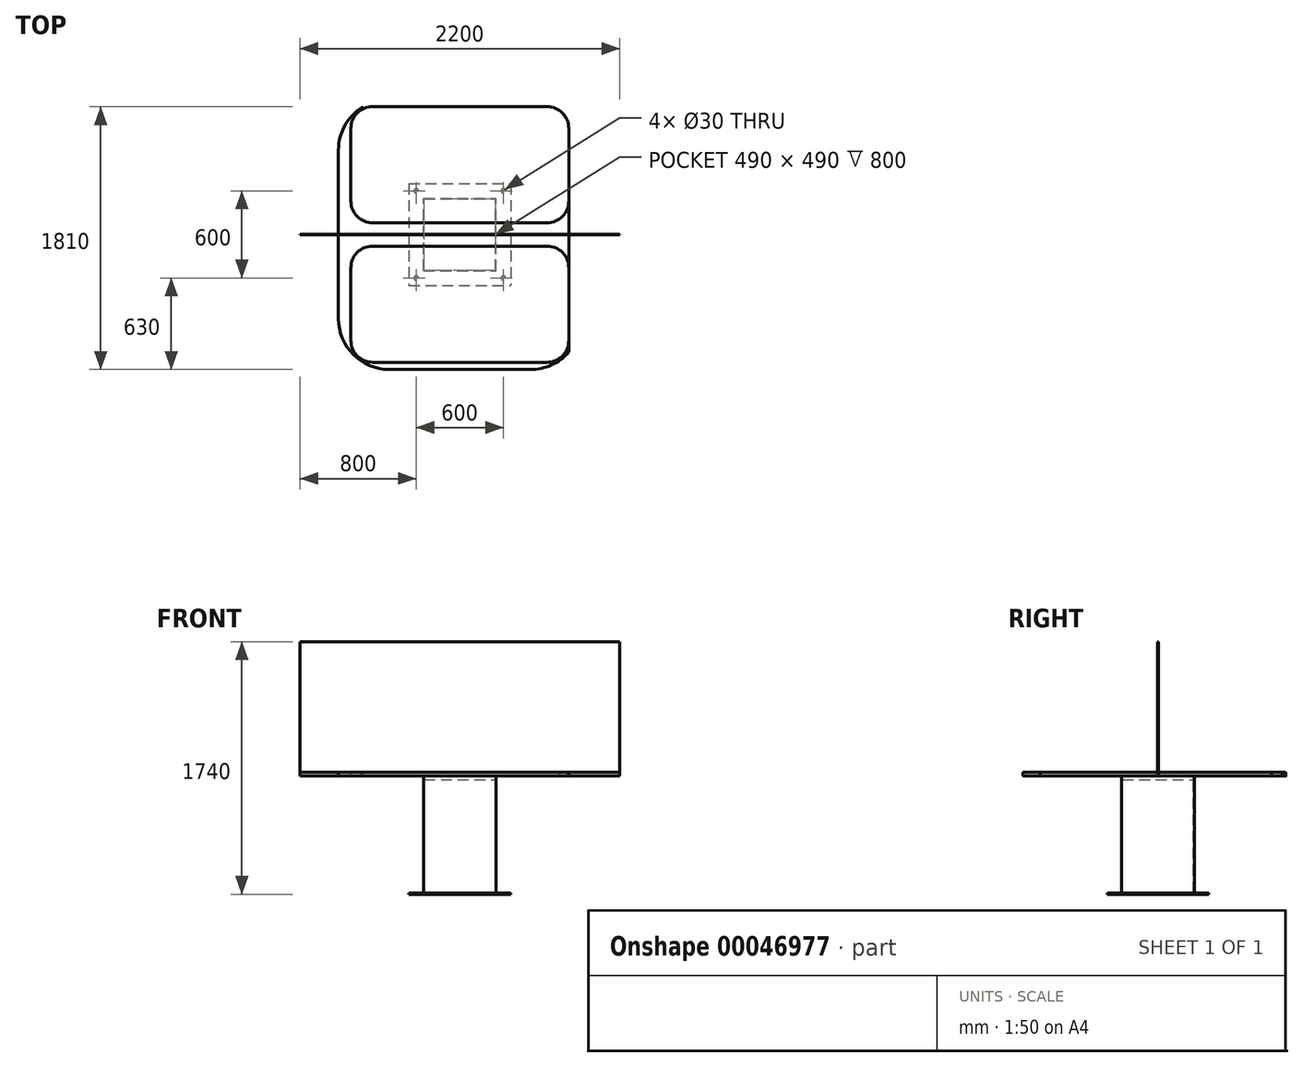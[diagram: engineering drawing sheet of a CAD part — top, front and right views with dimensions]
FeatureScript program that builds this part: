
annotation { "Feature Type Name" : "Feature", "Feature Type Description" : "" }
export const myFeature = defineFeature(function(context is Context, id is Id, definition is map)
    precondition{}
    {
        {
            var Q0;
            Q0=qCreatedBy(makeId("Top.planeOp"),FACE);
            var sketch = newSketch(context, id + "F0", { "sketchPlane" : qUnion([Q0])});
            skCircle(sketch, "E0", {"center": v(0, 0) * mm, "radius": 1250 * mm});
            skSolve(sketch);
        }
        {
            var Q0;
            Q0=qSketchRegion(id+"F0",true);
            extrude(context, id + "F1", {"entities" : qUnion([Q0]), "depth" : 25 * mm});
        }
        {
            var Q0;
            Q0=makeQuery(id+"F1.opExtrude","CAP_FACE",FACE,{"disambiguationData":[OSD([sQuery(id+"F0.wireOp",EDGE,"E0")])],"isStart":false});
            var sketch = newSketch(context, id + "F2", { "sketchPlane" : qUnion([Q0])});
            skLineSegment(sketch, "E1", {"start": v(0, 1250) * mm, "end": v(0, -1250) * mm, "construction": true});
            skLineSegment(sketch, "E2", {"start": v(149.27, 480) * mm, "end": v(0, 480) * mm, "construction": true});
            skLineSegment(sketch, "E3.MirrorCS", {"start": v(149.27, -480) * mm, "end": v(0, -480) * mm, "construction": true});
            skLineSegment(sketch, "E4.rect.bottom", {"start": v(600, 80) * mm, "end": v(-600, 80) * mm});
            skLineSegment(sketch, "E4.rect.top", {"start": v(600, 880) * mm, "end": v(-600, 880) * mm});
            skLineSegment(sketch, "E4.rect.left", {"start": v(750, 230) * mm, "end": v(750, 730) * mm});
            skLineSegment(sketch, "E4.rect.right", {"start": v(-750, 230) * mm, "end": v(-750, 730) * mm});
            skPoint(sketch, "E4.rect.middle", {"position": v(0, 480) * mm});
            skLineSegment(sketch, "E5.MirrorCS", {"start": v(-750, -230) * mm, "end": v(-750, -730) * mm});
            skLineSegment(sketch, "E6.MirrorCS", {"start": v(750, -230) * mm, "end": v(750, -730) * mm});
            skLineSegment(sketch, "E7.MirrorCS", {"start": v(600, -880) * mm, "end": v(-600, -880) * mm});
            skLineSegment(sketch, "E8.MirrorCS", {"start": v(600, -80) * mm, "end": v(-600, -80) * mm});
            skLineSegment(sketch, "E9.MirrorCS", {"start": v(149.27, -480) * mm, "end": v(0, -480) * mm});
            skPoint(sketch, "E10.MirrorP", {"position": v(0, -480) * mm});
            skPoint(sketch, "E11.visualSharp", {"position": v(-750, -880) * mm});
            skArc(sketch, "E11.filletArc", {"start": v(-750, -730) * mm, "mid": v(-706.07, -836.07) * mm, "end": v(-600, -880) * mm});
            skPoint(sketch, "E12.visualSharp", {"position": v(-750, -80) * mm});
            skArc(sketch, "E12.filletArc", {"start": v(-600, -80) * mm, "mid": v(-706.07, -123.93) * mm, "end": v(-750, -230) * mm});
            skPoint(sketch, "E13.visualSharp", {"position": v(750, -80) * mm});
            skArc(sketch, "E13.filletArc", {"start": v(750, -230) * mm, "mid": v(706.07, -123.93) * mm, "end": v(600, -80) * mm});
            skPoint(sketch, "E14.visualSharp", {"position": v(750, -880) * mm});
            skArc(sketch, "E14.filletArc", {"start": v(600, -880) * mm, "mid": v(706.07, -836.07) * mm, "end": v(750, -730) * mm});
            skPoint(sketch, "E15.visualSharp", {"position": v(-750, 80) * mm});
            skArc(sketch, "E15.filletArc", {"start": v(-750, 230) * mm, "mid": v(-706.07, 123.93) * mm, "end": v(-600, 80) * mm});
            skPoint(sketch, "E16.visualSharp", {"position": v(-750, 880) * mm});
            skArc(sketch, "E16.filletArc", {"start": v(-600, 880) * mm, "mid": v(-706.07, 836.07) * mm, "end": v(-750, 730) * mm});
            skPoint(sketch, "E17.visualSharp", {"position": v(750, 880) * mm});
            skArc(sketch, "E17.filletArc", {"start": v(750, 730) * mm, "mid": v(706.07, 836.07) * mm, "end": v(600, 880) * mm});
            skPoint(sketch, "E18.visualSharp", {"position": v(750, 80) * mm});
            skArc(sketch, "E18.filletArc", {"start": v(600, 80) * mm, "mid": v(706.07, 123.93) * mm, "end": v(750, 230) * mm});
            skSolve(sketch);
        }
        {
            var Q0;
            Q0=makeQuery(id+"F2.imprint","IMPRINT",FACE,{"disambiguationData":[TD([[makeQuery(id+"F2.imprint","IMPRINT",EDGE,{"derivedFrom":sQuery(id+"F2.wireOp",EDGE,"E4.rect.bottom")}),-1.0]])]});
            var Q1;
            Q1=makeQuery(id+"F2.imprint","IMPRINT",FACE,{"disambiguationData":[TD([[makeQuery(id+"F2.imprint","IMPRINT",EDGE,{"derivedFrom":sQuery(id+"F2.wireOp",EDGE,"E5.MirrorCS")}),1.0]])]});
            extrude(context, id + "F3", {"entities" : qUnion([Q0, Q1]), "operationType" : NewBodyOperationType.ADD, "depth" : 0.1 * mm});
        }
        {
            var Q0;
            Q0=makeQuery(id+"F1.opExtrude","CAP_FACE",FACE,{"disambiguationData":[OSD([sQuery(id+"F0.wireOp",EDGE,"E0")])],"isStart":true});
            var sketch = newSketch(context, id + "F4", { "sketchPlane" : qUnion([Q0])});
            skLineSegment(sketch, "E19.rect.bottom", {"start": v(-250, 250) * mm, "end": v(250, 250) * mm});
            skLineSegment(sketch, "E19.rect.top", {"start": v(-250, -250) * mm, "end": v(250, -250) * mm});
            skLineSegment(sketch, "E19.rect.left", {"start": v(-250, 250) * mm, "end": v(-250, -250) * mm});
            skLineSegment(sketch, "E19.rect.right", {"start": v(250, 250) * mm, "end": v(250, -250) * mm});
            skPoint(sketch, "E19.rect.middle", {"position": v(0, 0) * mm});
            skLineSegment(sketch, "E20.rect.bottom", {"start": v(-245, 245) * mm, "end": v(245, 245) * mm});
            skLineSegment(sketch, "E20.rect.top", {"start": v(-245, -245) * mm, "end": v(245, -245) * mm});
            skLineSegment(sketch, "E20.rect.left", {"start": v(-245, 245) * mm, "end": v(-245, -245) * mm});
            skLineSegment(sketch, "E20.rect.right", {"start": v(245, 245) * mm, "end": v(245, -245) * mm});
            skSolve(sketch);
        }
        {
            var Q0;
            Q0=makeQuery(id+"F4.imprint","IMPRINT",FACE,{"disambiguationData":[TD([[makeQuery(id+"F4.imprint","IMPRINT",EDGE,{"derivedFrom":sQuery(id+"F4.wireOp",EDGE,"E19.rect.bottom")}),-1.0]])]});
            extrude(context, id + "F5", {"entities" : qUnion([Q0]), "depth" : 800 * mm});
        }
        {
            var Q0;
            Q0=makeQuery(id+"F1.opExtrude","CAP_FACE",FACE,{"disambiguationData":[OSD([sQuery(id+"F0.wireOp",EDGE,"E0")])],"isStart":false});
            var sketch = newSketch(context, id + "F6", { "sketchPlane" : qUnion([Q0])});
            skLineSegment(sketch, "E21.rect.left", {"start": v(-1250, 2.5) * mm, "end": v(-1250, -2.5) * mm});
            skLineSegment(sketch, "E21.rect.right", {"start": v(1250, 2.5) * mm, "end": v(1250, -2.5) * mm});
            skPoint(sketch, "E21.rect.middle", {"position": v(0, 0) * mm});
            skLineSegment(sketch, "E22.rect.bottom", {"start": v(1100, -2.5) * mm, "end": v(-1100, -2.5) * mm});
            skLineSegment(sketch, "E22.rect.top", {"start": v(1100, 2.5) * mm, "end": v(-1100, 2.5) * mm});
            skLineSegment(sketch, "E22.rect.left", {"start": v(1100, -2.5) * mm, "end": v(1100, 2.5) * mm});
            skLineSegment(sketch, "E22.rect.right", {"start": v(-1100, -2.5) * mm, "end": v(-1100, 2.5) * mm});
            skSolve(sketch);
        }
        {
            var Q0;
            Q0=makeQuery(id+"F6.imprint","IMPRINT",FACE,{"disambiguationData":[TD([[makeQuery(id+"F6.imprint","IMPRINT",EDGE,{"derivedFrom":sQuery(id+"F6.wireOp",EDGE,"E21.rect.bottom")}),-1.0]])]});
            var Q1;
            Q1=makeQuery(id+"F6.imprint","IMPRINT",FACE,{"disambiguationData":[TD([[makeQuery(id+"F6.imprint","IMPRINT",EDGE,{"derivedFrom":sQuery(id+"F6.wireOp",EDGE,"E22.rect.bottom")}),-1.0]])]});
            extrude(context, id + "F7", {"entities" : qUnion([Q0, Q1]), "depth" : 900 * mm});
        }
        {
            var Q0;
            Q0=makeQuery(id+"F5.opExtrude","CAP_FACE",FACE,{"disambiguationData":[OSD([sQuery(id+"F4.wireOp",EDGE,"E19.rect.bottom"),sQuery(id+"F4.wireOp",EDGE,"E19.rect.top"),sQuery(id+"F4.wireOp",EDGE,"E19.rect.left"),sQuery(id+"F4.wireOp",EDGE,"E19.rect.right"),sQuery(id+"F4.wireOp",EDGE,"E20.rect.bottom"),sQuery(id+"F4.wireOp",EDGE,"E20.rect.top"),sQuery(id+"F4.wireOp",EDGE,"E20.rect.left"),sQuery(id+"F4.wireOp",EDGE,"E20.rect.right")])],"isStart":false});
            var sketch = newSketch(context, id + "F8", { "sketchPlane" : qUnion([Q0])});
            skLineSegment(sketch, "E23.bottom", {"start": v(-250, 250) * mm, "end": v(250, 250) * mm});
            skLineSegment(sketch, "E23.top", {"start": v(-250, -250) * mm, "end": v(250, -250) * mm});
            skLineSegment(sketch, "E23.left", {"start": v(-250, 250) * mm, "end": v(-250, -250) * mm});
            skLineSegment(sketch, "E23.right", {"start": v(250, 250) * mm, "end": v(250, -250) * mm});
            skSolve(sketch);
        }
        {
            var Q0;
            Q0=qSketchRegion(id+"F8",true);
            extrude(context, id + "F9", {"entities" : qUnion([Q0]), "operationType" : NewBodyOperationType.ADD, "depth" : 5 * mm});
        }
        {
            var Q0;
            Q0=makeQuery(id+"F9.opExtrude","CAP_FACE",FACE,{"disambiguationData":[OSD([sQuery(id+"F8.wireOp",EDGE,"E23.bottom"),sQuery(id+"F8.wireOp",EDGE,"E23.top"),sQuery(id+"F8.wireOp",EDGE,"E23.left"),sQuery(id+"F8.wireOp",EDGE,"E23.right")])],"isStart":false});
            var sketch = newSketch(context, id + "F10", { "sketchPlane" : qUnion([Q0])});
            skLineSegment(sketch, "E24.rect.bottom", {"start": v(-350, -350) * mm, "end": v(350, -350) * mm});
            skLineSegment(sketch, "E24.rect.top", {"start": v(-350, 350) * mm, "end": v(350, 350) * mm});
            skLineSegment(sketch, "E24.rect.left", {"start": v(-350, -350) * mm, "end": v(-350, 350) * mm});
            skLineSegment(sketch, "E24.rect.right", {"start": v(350, -350) * mm, "end": v(350, 350) * mm});
            skPoint(sketch, "E24.rect.middle", {"position": v(0, 0) * mm});
            skLineSegment(sketch, "E25.rect.bottom", {"start": v(-300, 300) * mm, "end": v(300, 300) * mm, "construction": true});
            skLineSegment(sketch, "E25.rect.top", {"start": v(-300, -300) * mm, "end": v(300, -300) * mm, "construction": true});
            skLineSegment(sketch, "E25.rect.left", {"start": v(-300, 300) * mm, "end": v(-300, -300) * mm, "construction": true});
            skLineSegment(sketch, "E25.rect.right", {"start": v(300, 300) * mm, "end": v(300, -300) * mm, "construction": true});
            skCircle(sketch, "E26", {"center": v(-300, 300) * mm, "radius": 15 * mm});
            skCircle(sketch, "E27", {"center": v(300, 300) * mm, "radius": 15 * mm});
            skCircle(sketch, "E28", {"center": v(300, -300) * mm, "radius": 15 * mm});
            skCircle(sketch, "E29", {"center": v(-300, -300) * mm, "radius": 15 * mm});
            skSolve(sketch);
        }
        {
            var Q0;
            Q0=qSketchRegion(id+"F10",true);
            extrude(context, id + "F11", {"entities" : qUnion([Q0]), "operationType" : NewBodyOperationType.ADD, "depth" : 10 * mm});
        }
        {
            var Q0;
            Q0=makeQuery(id+"F1.opExtrude","CAP_FACE",FACE,{"disambiguationData":[OSD([sQuery(id+"F0.wireOp",EDGE,"E0")])],"isStart":false});
            var sketch = newSketch(context, id + "F12", { "sketchPlane" : qUnion([Q0])});
            skLineSegment(sketch, "E30", {"start": v(1245, 930) * mm, "end": v(-1255, 930) * mm});
            skLineSegment(sketch, "E31", {"start": v(-1255, 930) * mm, "end": v(-1255, 1430) * mm});
            skLineSegment(sketch, "E32", {"start": v(-1255, 1430) * mm, "end": v(1245, 1430) * mm});
            skLineSegment(sketch, "E33", {"start": v(1245, 1430) * mm, "end": v(1245, 930) * mm});
            skLineSegment(sketch, "E34", {"start": v(0, 0) * mm, "end": v(209.4, 0) * mm});
            skLineSegment(sketch, "E35.MirrorCS", {"start": v(1245, -930) * mm, "end": v(-1255, -930) * mm});
            skLineSegment(sketch, "E36.MirrorCS", {"start": v(-1255, -930) * mm, "end": v(-1255, -1430) * mm});
            skLineSegment(sketch, "E37.MirrorCS", {"start": v(-1255, -1430) * mm, "end": v(1245, -1430) * mm});
            skLineSegment(sketch, "E38.MirrorCS", {"start": v(1245, -1430) * mm, "end": v(1245, -930) * mm});
            skSolve(sketch);
        }
        {
            var Q0;
            {var subQ5=sQuery(id+"F12.wireOp",EDGE,"E36.MirrorCS");Q0=makeQuery(id+"F12.imprint","IMPRINT",FACE,{"disambiguationData":[TD([[makeQuery(id+"F12.imprint","IMPRINT",EDGE,{"derivedFrom":subQ5}),1.0]])]});}
            var Q1;
            {var subQ0=makeQuery(id+"F1.opExtrude","CAP_EDGE",EDGE,{"disambiguationData":[OSD([sQuery(id+"F0.wireOp",EDGE,"E0")])],"isStart":false});var subQ1=sQuery(id+"F12.wireOp",EDGE,"E30");var subQ3=makeQuery(id+"F12.imprint","INTERSECT",VERTEX,{"disambiguationData":[OD(0.0)],"derivedFrom":[subQ0,subQ1]});Q1=makeQuery(id+"F12.imprint","IMPRINT",FACE,{"disambiguationData":[TD([[makeQuery(id+"F12.imprint","IMPRINT",EDGE,{"disambiguationData":[TD([[subQ3,-1.0]])],"derivedFrom":subQ1}),-1.0]])]});}
            var Q2;
            {var subQ0=makeQuery(id+"F1.opExtrude","CAP_EDGE",EDGE,{"disambiguationData":[OSD([sQuery(id+"F0.wireOp",EDGE,"E0")])],"isStart":false});var subQ1=sQuery(id+"F12.wireOp",EDGE,"E35.MirrorCS");var subQ3=makeQuery(id+"F12.imprint","INTERSECT",VERTEX,{"disambiguationData":[OD(0.0)],"derivedFrom":[subQ0,subQ1]});Q2=makeQuery(id+"F12.imprint","IMPRINT",FACE,{"disambiguationData":[TD([[makeQuery(id+"F12.imprint","IMPRINT",EDGE,{"disambiguationData":[TD([[subQ3,-1.0]])],"derivedFrom":subQ1}),1.0]])]});}
            extrude(context, id + "F13", {"entities" : qUnion([Q0, Q1, Q2]), "operationType" : NewBodyOperationType.REMOVE, "oppositeDirection" : true, "depth" : 30 * mm});
        }
        {
            var Q0;
            Q0=makeQuery(id+"F1.opExtrude","CAP_FACE",FACE,{"disambiguationData":[OSD([sQuery(id+"F0.wireOp",EDGE,"E0")])],"isStart":false});
            var sketch = newSketch(context, id + "F14", { "sketchPlane" : qUnion([Q0])});
            skLineSegment(sketch, "E39", {"start": v(835.22, -930) * mm, "end": v(835.22, 930) * mm});
            skLineSegment(sketch, "E40", {"start": v(835.22, 930) * mm, "end": v(1324.29, 930) * mm});
            skLineSegment(sketch, "E41", {"start": v(1324.29, 930) * mm, "end": v(1324.29, -826) * mm});
            skLineSegment(sketch, "E42", {"start": v(1324.29, -826) * mm, "end": v(835.22, -930) * mm});
            skLineSegment(sketch, "E43.MirrorCS", {"start": v(-835.22, -930) * mm, "end": v(-835.22, 930) * mm});
            skLineSegment(sketch, "E44.MirrorCS", {"start": v(-835.22, 930) * mm, "end": v(-1324.29, 930) * mm});
            skLineSegment(sketch, "E45.MirrorCS", {"start": v(-1324.29, 930) * mm, "end": v(-1324.29, -826) * mm});
            skLineSegment(sketch, "E46.MirrorCS", {"start": v(-1324.29, -826) * mm, "end": v(-835.22, -930) * mm});
            skSolve(sketch);
        }
        {
            var Q0;
            Q0=qSketchRegion(id+"F14",true);
            extrude(context, id + "F15", {"entities" : qUnion([Q0]), "operationType" : NewBodyOperationType.REMOVE, "oppositeDirection" : true, "depth" : 30 * mm});
        }
        {
            var Q0;
            Q0=makeQuery(id+"F5.opExtrude","CAP_FACE",FACE,{"disambiguationData":[OSD([sQuery(id+"F4.wireOp",EDGE,"E19.rect.bottom"),sQuery(id+"F4.wireOp",EDGE,"E19.rect.top"),sQuery(id+"F4.wireOp",EDGE,"E19.rect.left"),sQuery(id+"F4.wireOp",EDGE,"E19.rect.right"),sQuery(id+"F4.wireOp",EDGE,"E20.rect.bottom"),sQuery(id+"F4.wireOp",EDGE,"E20.rect.top"),sQuery(id+"F4.wireOp",EDGE,"E20.rect.left"),sQuery(id+"F4.wireOp",EDGE,"E20.rect.right")])],"isStart":true});
            var sketch = newSketch(context, id + "F16", { "sketchPlane" : qUnion([Q0])});
            skLineSegment(sketch, "E47.bottom", {"start": v(-245, 245) * mm, "end": v(245, 245) * mm});
            skLineSegment(sketch, "E47.top", {"start": v(-245, -245) * mm, "end": v(245, -245) * mm});
            skLineSegment(sketch, "E47.left", {"start": v(-245, 245) * mm, "end": v(-245, -245) * mm});
            skLineSegment(sketch, "E47.right", {"start": v(245, 245) * mm, "end": v(245, -245) * mm});
            skSolve(sketch);
        }
        {
            var Q0;
            Q0=qSketchRegion(id+"F16",true);
            extrude(context, id + "F17", {"entities" : qUnion([Q0]), "oppositeDirection" : true, "depth" : 25 * mm});
        }
        {
            var Q0;
            {var subQ0=sQuery(id+"F0.wireOp",EDGE,"E0");var subQ1=sQuery(id+"F12.wireOp",EDGE,"E30");Q0=makeQuery(id+"F15.boolean.opBoolean","MERGE",EDGE,{"derivedFrom":[makeQuery(id+"F13.boolean.opBoolean","COPY",EDGE,{"derivedFrom":makeQuery(id+"F13.opExtrude","SWEPT_EDGE",EDGE,{"disambiguationData":[OSD([subQ0,subQ1]),TDD([makeQuery(id+"F12.imprint","INTERSECT",VERTEX,{"disambiguationData":[OD(1.0)],"derivedFrom":[makeQuery(id+"F1.opExtrude","CAP_EDGE",EDGE,{"disambiguationData":[OSD([subQ0])],"isStart":false}),subQ1]})])]})}),makeQuery(id+"F15.opExtrude","SWEPT_EDGE",EDGE,{"disambiguationData":[OSD([subQ0,subQ1,sQuery(id+"F14.wireOp",EDGE,"E43.MirrorCS"),sQuery(id+"F14.wireOp",EDGE,"E44.MirrorCS")])]})]});}
            var Q1;
            {var subQ0=sQuery(id+"F0.wireOp",EDGE,"E0");var subQ1=sQuery(id+"F12.wireOp",EDGE,"E35.MirrorCS");Q1=makeQuery(id+"F15.boolean.opBoolean","MERGE",EDGE,{"derivedFrom":[makeQuery(id+"F13.boolean.opBoolean","INTERSECT",EDGE,{"disambiguationData":[OD(1.0)],"derivedFrom":[makeQuery(id+"F1.opExtrude","SWEPT_FACE",FACE,{"disambiguationData":[OSD([subQ0])]}),makeQuery(id+"F13.opExtrude","SWEPT_FACE",FACE,{"disambiguationData":[OSD([subQ1])]})]}),makeQuery(id+"F15.opExtrude","SWEPT_EDGE",EDGE,{"disambiguationData":[OSD([subQ0,subQ1,sQuery(id+"F14.wireOp",EDGE,"E43.MirrorCS"),sQuery(id+"F14.wireOp",EDGE,"E46.MirrorCS")])]})]});}
            var Q2;
            {var subQ0=sQuery(id+"F0.wireOp",EDGE,"E0");var subQ1=sQuery(id+"F12.wireOp",EDGE,"E35.MirrorCS");Q2=makeQuery(id+"F15.boolean.opBoolean","MERGE",EDGE,{"derivedFrom":[makeQuery(id+"F13.boolean.opBoolean","INTERSECT",EDGE,{"disambiguationData":[OD(0.0)],"derivedFrom":[makeQuery(id+"F1.opExtrude","SWEPT_FACE",FACE,{"disambiguationData":[OSD([subQ0])]}),makeQuery(id+"F13.opExtrude","SWEPT_FACE",FACE,{"disambiguationData":[OSD([subQ1])]})]}),makeQuery(id+"F15.opExtrude","SWEPT_EDGE",EDGE,{"disambiguationData":[OSD([subQ0,subQ1,sQuery(id+"F14.wireOp",EDGE,"E39"),sQuery(id+"F14.wireOp",EDGE,"E42")])]})]});}
            var Q3;
            {var subQ0=sQuery(id+"F0.wireOp",EDGE,"E0");var subQ1=sQuery(id+"F12.wireOp",EDGE,"E30");Q3=makeQuery(id+"F15.boolean.opBoolean","MERGE",EDGE,{"derivedFrom":[makeQuery(id+"F13.boolean.opBoolean","COPY",EDGE,{"derivedFrom":makeQuery(id+"F13.opExtrude","SWEPT_EDGE",EDGE,{"disambiguationData":[OSD([subQ0,subQ1]),TDD([makeQuery(id+"F12.imprint","INTERSECT",VERTEX,{"disambiguationData":[OD(0.0)],"derivedFrom":[makeQuery(id+"F1.opExtrude","CAP_EDGE",EDGE,{"disambiguationData":[OSD([subQ0])],"isStart":false}),subQ1]})])]})}),makeQuery(id+"F15.opExtrude","SWEPT_EDGE",EDGE,{"disambiguationData":[OSD([subQ0,subQ1,sQuery(id+"F14.wireOp",EDGE,"E39"),sQuery(id+"F14.wireOp",EDGE,"E40")])]})]});}
            fillet(context, id + "F18", {"entities" : qUnion([Q0, Q1, Q2, Q3]), "radius" : 350 * mm, "tangentPropagation" : true, "allowEdgeOverflow" : false});
        }
        {
            var Q0;
            Q0=makeQuery(id+"F1.opExtrude","CAP_FACE",FACE,{"disambiguationData":[OSD([sQuery(id+"F0.wireOp",EDGE,"E0")])],"isStart":false});
            var sketch = newSketch(context, id + "F19", { "sketchPlane" : qUnion([Q0])});
            skLineSegment(sketch, "E48", {"start": v(-750, 730) * mm, "end": v(-750, -730) * mm});
            skLineSegment(sketch, "E49", {"start": v(-750, -730) * mm, "end": v(-750, -880) * mm});
            skLineSegment(sketch, "E50", {"start": v(-750, -880) * mm, "end": v(750, -880) * mm});
            skLineSegment(sketch, "E51", {"start": v(750, -880) * mm, "end": v(750, 769.39) * mm});
            skLineSegment(sketch, "E52", {"start": v(-600, 880) * mm, "end": v(665.5, 880) * mm});
            skLineSegment(sketch, "E53", {"start": v(665.5, 880) * mm, "end": v(750, 769.39) * mm});
            skLineSegment(sketch, "E54", {"start": v(-600, 880) * mm, "end": v(-665.5, 880) * mm});
            skLineSegment(sketch, "E55", {"start": v(-665.5, 880) * mm, "end": v(-750, 730) * mm});
            skSolve(sketch);
        }
        {
            var Q0;
            {var subQ2=sQuery(id+"F14.wireOp",EDGE,"E43.MirrorCS");var subQ7=makeQuery(id+"F15.boolean.opBoolean","COPY",EDGE,{"derivedFrom":makeQuery(id+"F15.opExtrude","CAP_EDGE",EDGE,{"disambiguationData":[OSD([subQ2])],"isStart":true})});Q0=makeQuery(id+"F19.imprint","IMPRINT",FACE,{"disambiguationData":[TD([[makeQuery(id+"F19.imprint","IMPRINT",EDGE,{"derivedFrom":subQ7}),-1.0]])]});}
            var Q1;
            {var subQ5=sQuery(id+"F19.wireOp",EDGE,"E54");Q1=makeQuery(id+"F19.imprint","IMPRINT",FACE,{"disambiguationData":[TD([[makeQuery(id+"F19.imprint","IMPRINT",EDGE,{"derivedFrom":subQ5}),-1.0]])]});}
            var Q2;
            {var subQ8=sQuery(id+"F19.wireOp",EDGE,"E53");Q2=makeQuery(id+"F19.imprint","IMPRINT",FACE,{"disambiguationData":[TD([[makeQuery(id+"F19.imprint","IMPRINT",EDGE,{"derivedFrom":subQ8}),1.0]])]});}
            var Q3;
            {var subQ2=sQuery(id+"F12.wireOp",EDGE,"E35.MirrorCS");var subQ8=makeQuery(id+"F13.boolean.opBoolean","COPY",EDGE,{"derivedFrom":makeQuery(id+"F13.opExtrude","CAP_EDGE",EDGE,{"disambiguationData":[OSD([subQ2])],"isStart":true})});Q3=makeQuery(id+"F19.imprint","IMPRINT",FACE,{"disambiguationData":[TD([[makeQuery(id+"F19.imprint","IMPRINT",EDGE,{"derivedFrom":subQ8}),-1.0]])]});}
            var Q4;
            {var subQ7=makeQuery(id+"F3.opExtrude","CAP_EDGE",EDGE,{"disambiguationData":[OSD([sQuery(id+"F2.wireOp",EDGE,"E14.filletArc")])],"isStart":true});Q4=makeQuery(id+"F19.imprint","IMPRINT",FACE,{"disambiguationData":[TD([[makeQuery(id+"F19.imprint","IMPRINT",EDGE,{"derivedFrom":subQ7}),-1.0]])]});}
            var Q5;
            {var subQ1=sQuery(id+"F19.wireOp",EDGE,"E53");Q5=makeQuery(id+"F19.imprint","IMPRINT",FACE,{"disambiguationData":[TD([[makeQuery(id+"F19.imprint","IMPRINT",EDGE,{"derivedFrom":subQ1}),-1.0]])]});}
            var Q6;
            {var subQ3=sQuery(id+"F19.wireOp",EDGE,"E54");Q6=makeQuery(id+"F19.imprint","IMPRINT",FACE,{"disambiguationData":[TD([[makeQuery(id+"F19.imprint","IMPRINT",EDGE,{"derivedFrom":subQ3}),1.0]])]});}
            var Q7;
            {var subQ7=makeQuery(id+"F3.opExtrude","CAP_EDGE",EDGE,{"disambiguationData":[OSD([sQuery(id+"F2.wireOp",EDGE,"E11.filletArc")])],"isStart":true});Q7=makeQuery(id+"F19.imprint","IMPRINT",FACE,{"disambiguationData":[TD([[makeQuery(id+"F19.imprint","IMPRINT",EDGE,{"derivedFrom":subQ7}),-1.0]])]});}
            extrude(context, id + "F20", {"entities" : qUnion([Q0, Q1, Q2, Q3, Q4, Q5, Q6, Q7]), "operationType" : NewBodyOperationType.REMOVE, "oppositeDirection" : true, "depth" : 25 * mm});
        }
        {
            var Q0;
            Q0=makeQuery(id+"F7.opExtrude","SWEPT_FACE",FACE,{"disambiguationData":[OSD([sQuery(id+"F6.wireOp",EDGE,"E22.rect.bottom")])]});
            var sketch = newSketch(context, id + "F21", { "sketchPlane" : qUnion([Q0])});
            skLineSegment(sketch, "E56", {"start": v(-1100, 25) * mm, "end": v(-1100, 0) * mm});
            skLineSegment(sketch, "E57", {"start": v(-1100, 0) * mm, "end": v(-750, 0) * mm});
            skLineSegment(sketch, "E58", {"start": v(-750, 0) * mm, "end": v(-750, 25) * mm});
            skLineSegment(sketch, "E59", {"start": v(-1100, 25) * mm, "end": v(-750, 25) * mm});
            skLineSegment(sketch, "E60.MirrorCS", {"start": v(750, 0) * mm, "end": v(750, 25) * mm});
            skLineSegment(sketch, "E61.MirrorCS", {"start": v(1100, 25) * mm, "end": v(1100, 0) * mm});
            skLineSegment(sketch, "E62.MirrorCS", {"start": v(1100, 25) * mm, "end": v(750, 25) * mm});
            skLineSegment(sketch, "E63.MirrorCS", {"start": v(1100, 0) * mm, "end": v(750, 0) * mm});
            skSolve(sketch);
        }
        {
            var Q0;
            Q0=qSketchRegion(id+"F21",true);
            extrude(context, id + "F22", {"entities" : qUnion([Q0]), "oppositeDirection" : true, "depth" : 5 * mm});
        }
    });
